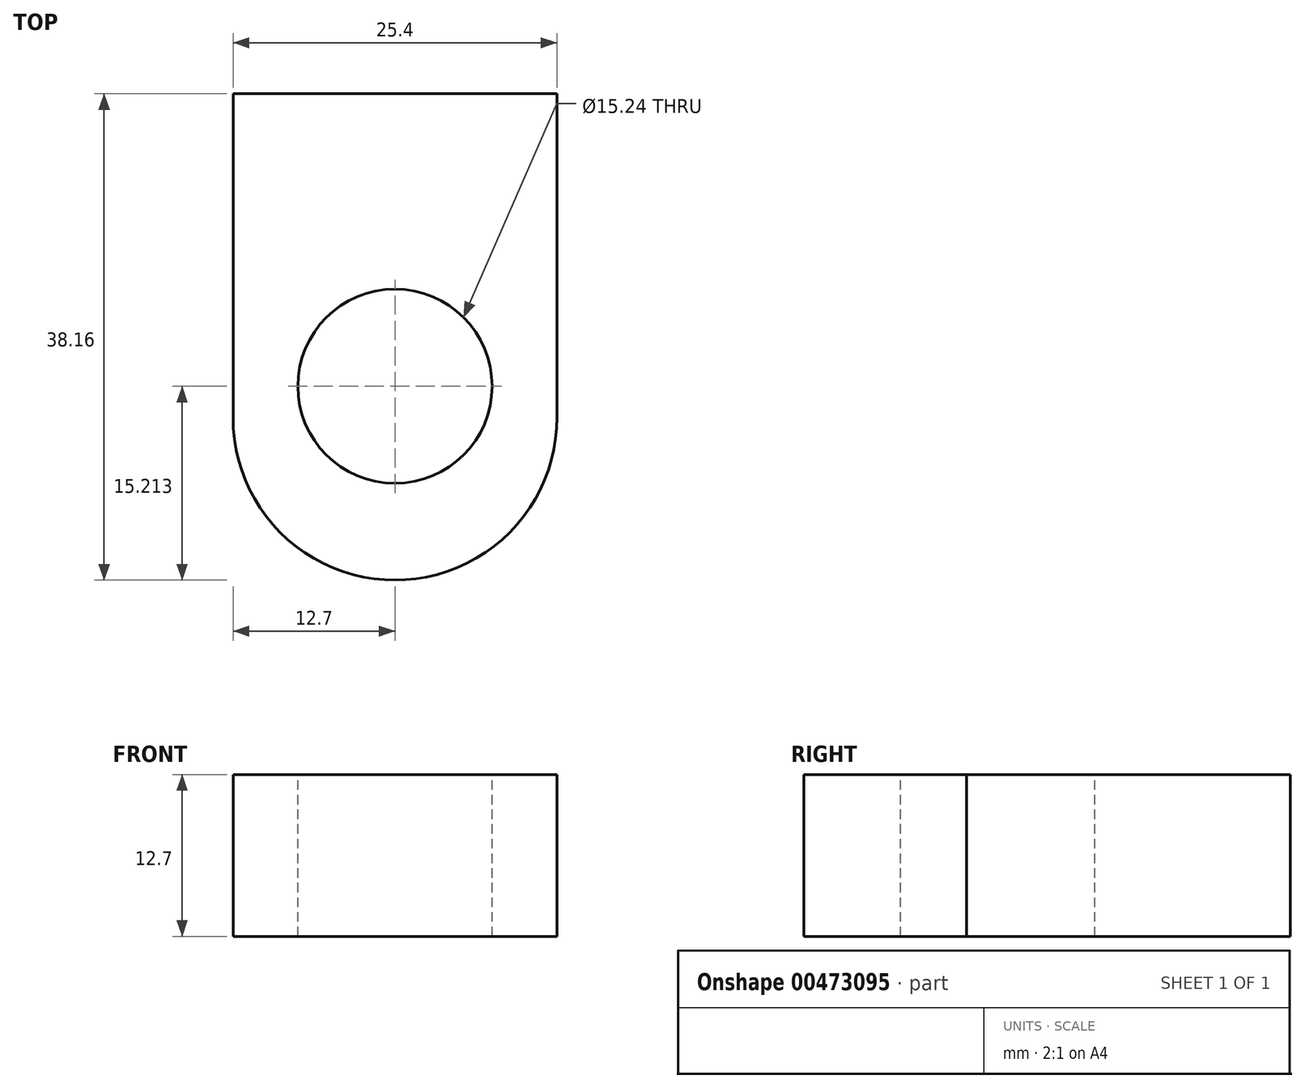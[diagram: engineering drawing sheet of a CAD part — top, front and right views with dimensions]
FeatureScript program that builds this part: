
annotation { "Feature Type Name" : "Feature", "Feature Type Description" : "" }
export const myFeature = defineFeature(function(context is Context, id is Id, definition is map)
    precondition{}
    {
        {
            var Q0;
            Q0=qCreatedBy(makeId("Top.planeOp"),FACE);
            var sketch = newSketch(context, id + "F0", { "sketchPlane" : qUnion([Q0])});
            skLineSegment(sketch, "E0.bottom", {"start": v(12.7, -12.7) * mm, "end": v(-12.7, -12.7) * mm});
            skLineSegment(sketch, "E0.top", {"start": v(12.7, 12.7) * mm, "end": v(-12.7, 12.7) * mm});
            skLineSegment(sketch, "E0.left", {"start": v(12.7, -12.7) * mm, "end": v(12.7, 12.7) * mm});
            skLineSegment(sketch, "E0.right", {"start": v(-12.7, -12.7) * mm, "end": v(-12.7, 12.7) * mm});
            skPoint(sketch, "E0.middle", {"position": v(0, 0) * mm});
            skSolve(sketch);
        }
        {
            var Q0;
            Q0=makeQuery(id+"F0.imprint","IMPRINT",FACE,{"disambiguationData":[TD([[makeQuery(id+"F0.imprint","IMPRINT",EDGE,{"derivedFrom":sQuery(id+"F0.wireOp",EDGE,"E0.bottom")}),-1.0]])]});
            extrude(context, id + "F1", {"entities" : qUnion([Q0]), "depth" : 12.7 * mm});
        }
        {
            var Q0;
            Q0=qCreatedBy(makeId("Top.planeOp"),FACE);
            var sketch = newSketch(context, id + "F2", { "sketchPlane" : qUnion([Q0])});
            skCircle(sketch, "E1", {"center": v(0, -12.76) * mm, "radius": 12.7 * mm});
            skSolve(sketch);
        }
        {
            var Q0;
            Q0 = qSketchRegion(id + "F2", true);
            extrude(context, id + "F3", {"entities" : qUnion([Q0]), "operationType" : NewBodyOperationType.ADD, "depth" : 12.7 * mm});
        }
        {
            var Q0;
            Q0=makeQuery(id+"F3.boolean.opBoolean","MERGE",FACE,{"derivedFrom":[makeQuery(id+"F1.opExtrude","CAP_FACE",FACE,{"disambiguationData":[OSD([sQuery(id+"F0.wireOp",EDGE,"E0.bottom"),sQuery(id+"F0.wireOp",EDGE,"E0.top"),sQuery(id+"F0.wireOp",EDGE,"E0.left"),sQuery(id+"F0.wireOp",EDGE,"E0.right")])],"isStart":false}),makeQuery(id+"F3.opExtrude","CAP_FACE",FACE,{"disambiguationData":[OSD([sQuery(id+"F2.wireOp",EDGE,"E1")])],"isStart":false})]});
            var sketch = newSketch(context, id + "F4", { "sketchPlane" : qUnion([Q0])});
            skCircle(sketch, "E2", {"center": v(0, -10.25) * mm, "radius": 7.62 * mm});
            skSolve(sketch);
        }
        {
            var Q0;
            Q0 = qSketchRegion(id + "F4", true);
            extrude(context, id + "F5", {"entities" : qUnion([Q0]), "operationType" : NewBodyOperationType.REMOVE, "endBound" : BoundingType.THROUGH_ALL, "oppositeDirection" : true, "depth" : 25.4 * mm});
        }
    });
